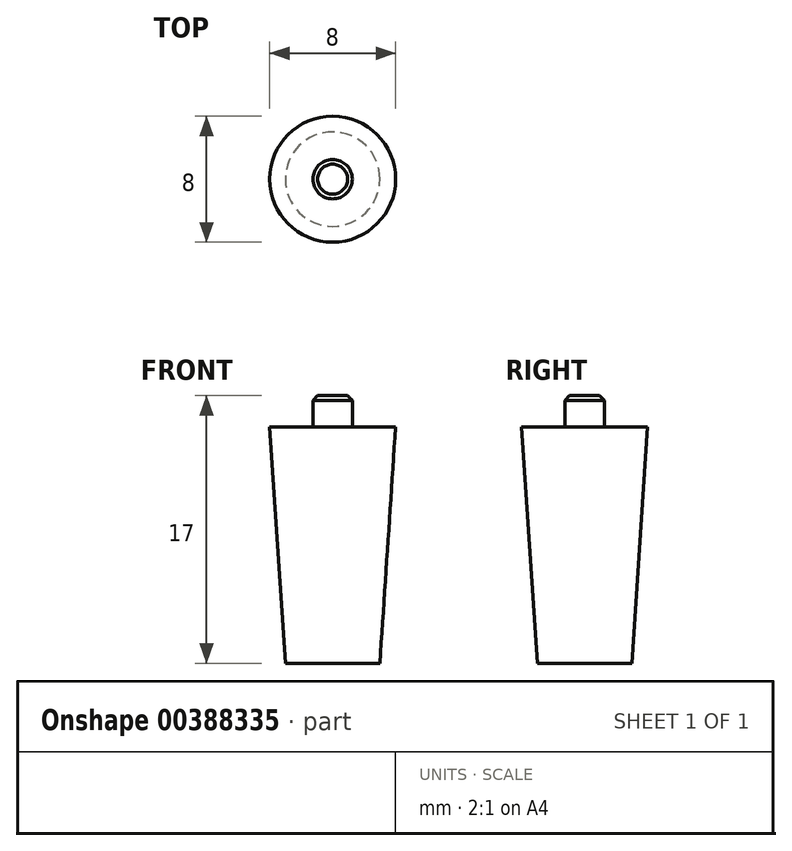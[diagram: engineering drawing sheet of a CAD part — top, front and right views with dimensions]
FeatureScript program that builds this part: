
annotation { "Feature Type Name" : "Feature", "Feature Type Description" : "" }
export const myFeature = defineFeature(function(context is Context, id is Id, definition is map)
    precondition{}
    {
        {
            var Q0;
            Q0=qCreatedBy(makeId("Front.planeOp"),FACE);
            var sketch = newSketch(context, id + "F0", { "sketchPlane" : qUnion([Q0])});
            skLineSegment(sketch, "E0", {"start": v(0, 0) * mm, "end": v(0, -15) * mm});
            skLineSegment(sketch, "E1", {"start": v(0, -15) * mm, "end": v(-3, -15) * mm});
            skLineSegment(sketch, "E2", {"start": v(-4, 0) * mm, "end": v(0, 0) * mm});
            skLineSegment(sketch, "E3", {"start": v(0, 5.07) * mm, "end": v(0, -18.59) * mm, "construction": true});
            skLineSegment(sketch, "E4", {"start": v(-4, 0) * mm, "end": v(-3, -15) * mm});
            skSolve(sketch);
        }
        {
            var Q0;
            Q0 = qSketchRegion(id + "F0", true);
            var Q1;
            Q1=sQuery(id+"F0.wireOp",EDGE,"E3");
            revolve(context, id + "F1", {"entities" : qUnion([Q0]), "axis" : qUnion([Q1]), "revolveType" : RevolveType.FULL});
        }
        {
            var Q0;
            Q0=makeQuery(id+"F1.opRevolve","SWEPT_FACE",FACE,{"disambiguationData":[OSD([sQuery(id+"F0.wireOp",EDGE,"E2")])]});
            var sketch = newSketch(context, id + "F2", { "sketchPlane" : qUnion([Q0])});
            skCircle(sketch, "E5", {"center": v(0, 0) * mm, "radius": 1.25 * mm});
            skSolve(sketch);
        }
        {
            var Q0;
            Q0 = qSketchRegion(id + "F2", true);
            extrude(context, id + "F3", {"entities" : qUnion([Q0]), "operationType" : NewBodyOperationType.ADD, "depth" : 2 * mm});
        }
        {
            var Q0;
            Q0=makeQuery(id+"F3.opExtrude","CAP_EDGE",EDGE,{"disambiguationData":[OSD([sQuery(id+"F2.wireOp",EDGE,"E5")])],"isStart":false});
            chamfer(context, id + "F4", {"entities" : qUnion([Q0]), "width" : 0.3 * mm, "tangentPropagation" : true});
        }
    });
